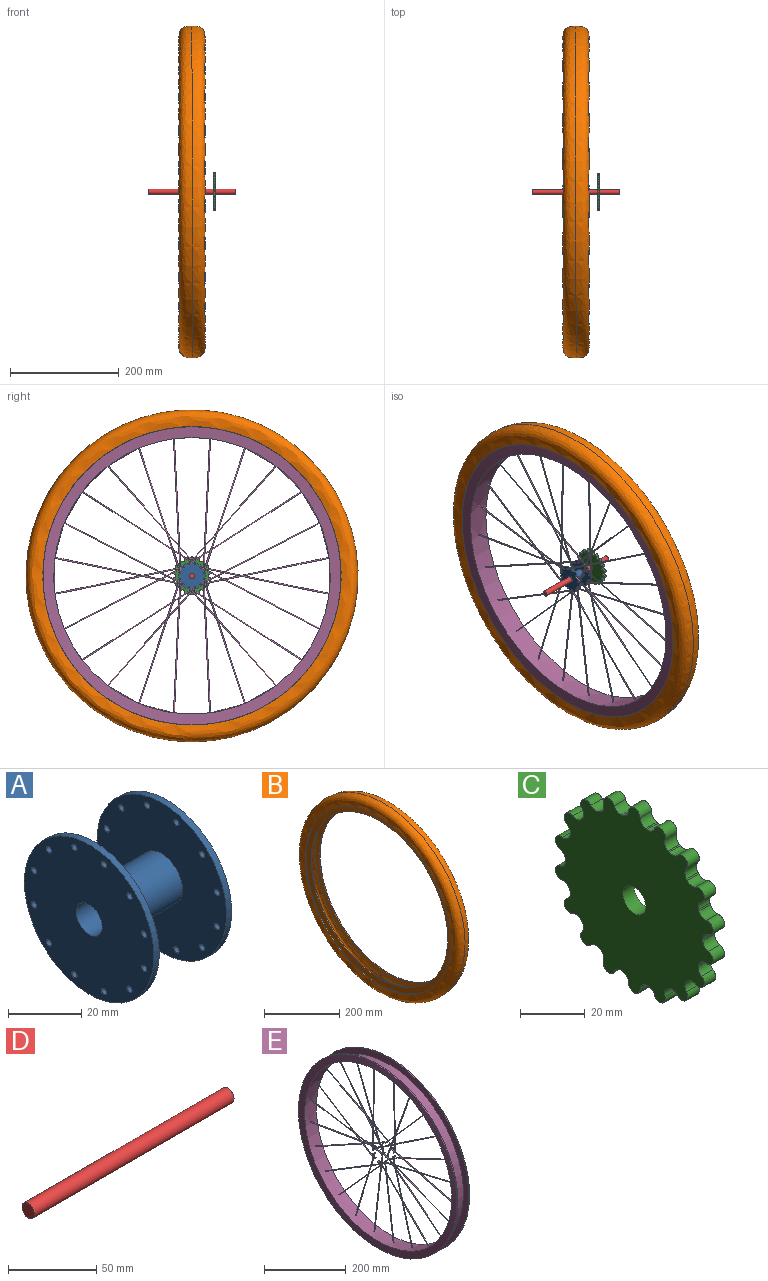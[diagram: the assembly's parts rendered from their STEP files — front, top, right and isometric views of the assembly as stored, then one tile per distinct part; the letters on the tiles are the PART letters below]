
ASSEMBLY  parts=5 mates=4
PART A: 32 faces, bbox 30x50x50 mm
  f0: cylinder r=8mm len=26mm, axis (-1,0,0), area 1306.9mm2, adj f4,f19
  f1: cylinder r=5mm len=30mm, axis (-1,0,0), area 942.5mm2, adj f2,f17
  f2: plane 50x50mm, normal (1,0,0), area 1847.3mm2, adj f1,f3,f5,f6,f7,f8,f9,f10
  f3: cylinder r=25mm len=50mm, axis (1,0,0), area 314.2mm2, adj f2,f4
  f4: plane 50x50mm, normal (-1,0,0), area 1724.7mm2, adj f0,f3,f5,f6,f7,f8,f9,f10
  f5: cylinder r=1mm len=2mm, axis (1,0,0), area 12.6mm2, adj f2,f4
  f6: cylinder r=1mm len=2mm, axis (1,0,0), area 12.6mm2, adj f2,f4
  f7: cylinder r=1mm len=2mm, axis (1,0,0), area 12.6mm2, adj f2,f4
  f8: cylinder r=1mm len=2mm, axis (1,0,0), area 12.6mm2, adj f2,f4
  f9: cylinder r=1mm len=2mm, axis (1,0,0), area 12.6mm2, adj f2,f4
  f10: cylinder r=1mm len=2mm, axis (1,0,0), area 12.6mm2, adj f2,f4
  f11: cylinder r=1mm len=2mm, axis (1,0,0), area 12.6mm2, adj f2,f4
  f12: cylinder r=1mm len=2mm, axis (1,0,0), area 12.6mm2, adj f2,f4
  f13: cylinder r=1mm len=2mm, axis (1,0,0), area 12.6mm2, adj f2,f4
  f14: cylinder r=1mm len=2mm, axis (1,0,0), area 12.6mm2, adj f2,f4
  f15: cylinder r=1mm len=2mm, axis (1,0,0), area 12.6mm2, adj f2,f4
  f16: cylinder r=1mm len=2mm, axis (1,0,0), area 12.6mm2, adj f2,f4
  f17: plane 50x50mm, normal (-1,0,0), area 1847.3mm2, adj f1,f18,f20,f21,f22,f23,f24,f25
  f18: cylinder r=25mm len=50mm, axis (-1,0,0), area 314.2mm2, adj f17,f19
  f19: plane 50x50mm, normal (1,0,0), area 1724.7mm2, adj f0,f18,f20,f21,f22,f23,f24,f25
  f20: cylinder r=1mm len=2mm, axis (-1,0,0), area 12.6mm2, adj f17,f19
  f21: cylinder r=1mm len=2mm, axis (-1,0,0), area 12.6mm2, adj f17,f19
  f22: cylinder r=1mm len=2mm, axis (-1,0,0), area 12.6mm2, adj f17,f19
  f23: cylinder r=1mm len=2mm, axis (-1,0,0), area 12.6mm2, adj f17,f19
  f24: cylinder r=1mm len=2mm, axis (-1,0,0), area 12.6mm2, adj f17,f19
  f25: cylinder r=1mm len=2mm, axis (-1,0,0), area 12.6mm2, adj f17,f19
  f26: cylinder r=1mm len=2mm, axis (-1,0,0), area 12.6mm2, adj f17,f19
  f27: cylinder r=1mm len=2mm, axis (-1,0,0), area 12.6mm2, adj f17,f19
  f28: cylinder r=1mm len=2mm, axis (-1,0,0), area 12.6mm2, adj f17,f19
  f29: cylinder r=1mm len=2mm, axis (-1,0,0), area 12.6mm2, adj f17,f19
  f30: cylinder r=1mm len=2mm, axis (-1,0,0), area 12.6mm2, adj f17,f19
  f31: cylinder r=1mm len=2mm, axis (-1,0,0), area 12.6mm2, adj f17,f19
PART B: 12 faces, bbox 48.1x610x610 mm
  f0: cone r=274.19mm half-angle=85deg, axis (-1,0,0), area 28787.9mm2, adj f1,f9
  f1: cylinder r=257mm len=514mm, axis (1,0,0), area 4862.8mm2, adj f0,f2
  f2: cone r=274.45mm half-angle=85deg, axis (-1,0,0), area 29240.3mm2, adj f1,f3
  f3: revolved ~598x598mm, area 68230.7mm2, adj f2,f4
  f4: revolved ~598x598mm, area 68230.7mm2, adj f3,f5
  f5: cone r=274.45mm half-angle=85deg, axis (1,0,0), area 29240.3mm2, adj f4,f6
  f6: cylinder r=257mm len=514mm, axis (1,0,0), area 4862.8mm2, adj f5,f7
  f7: cone r=274.19mm half-angle=85deg, axis (1,0,0), area 28787.9mm2, adj f6,f10
  f8: revolved ~610x610mm, area 87460.3mm2, adj f9,f11
  f9: cone r=273.92mm half-angle=5deg, axis (1,0,0), area 5165.8mm2, adj f0,f8
  f10: cone r=274.19mm half-angle=5deg, axis (-1,0,0), area 5165.8mm2, adj f7,f11
  f11: revolved ~610x610mm, area 87460.3mm2, adj f8,f10
PART C: 75 faces, bbox 5x69x70 mm
  f0: cylinder r=2.5mm len=5mm, axis (-1,0,0), area 39.3mm2, adj f1,f71,f73,f74
  f1: cylinder r=2.95mm len=5mm, axis (-1,0,0), area 20.7mm2, adj f0,f2,f73,f74
  f2: cylinder r=30mm len=5mm, axis (-1,0,0), area 2.5mm2, adj f1,f3,f73,f74
  f3: cylinder r=2.95mm len=5mm, axis (-1,0,0), area 20.7mm2, adj f2,f4,f73,f74
  f4: cylinder r=2.5mm len=5mm, axis (-1,0,0), area 39.3mm2, adj f3,f5,f73,f74
  f5: cylinder r=2.95mm len=5mm, axis (-1,0,0), area 20.7mm2, adj f4,f6,f73,f74
  f6: cylinder r=30mm len=5mm, axis (-1,0,0), area 2.5mm2, adj f5,f7,f73,f74
  f7: cylinder r=2.95mm len=5mm, axis (-1,0,0), area 20.7mm2, adj f6,f8,f73,f74
  f8: cylinder r=2.5mm len=5mm, axis (-1,0,0), area 39.3mm2, adj f7,f9,f73,f74
  f9: cylinder r=2.95mm len=5mm, axis (-1,0,0), area 20.7mm2, adj f8,f10,f73,f74
  f10: cylinder r=30mm len=5mm, axis (-1,0,0), area 2.5mm2, adj f9,f11,f73,f74
  f11: cylinder r=2.95mm len=5mm, axis (-1,0,0), area 20.7mm2, adj f10,f12,f73,f74
  f12: cylinder r=2.5mm len=5mm, axis (-1,0,0), area 39.3mm2, adj f11,f13,f73,f74
  f13: cylinder r=2.95mm len=5mm, axis (-1,0,0), area 20.7mm2, adj f12,f14,f73,f74
  f14: cylinder r=30mm len=5mm, axis (-1,0,0), area 2.5mm2, adj f13,f15,f73,f74
  f15: cylinder r=2.95mm len=5mm, axis (-1,0,0), area 20.7mm2, adj f14,f16,f73,f74
  f16: cylinder r=2.5mm len=5mm, axis (-1,0,0), area 39.3mm2, adj f15,f17,f73,f74
  f17: cylinder r=2.95mm len=5mm, axis (-1,0,0), area 20.7mm2, adj f16,f18,f73,f74
  f18: cylinder r=30mm len=5mm, axis (-1,0,0), area 2.5mm2, adj f17,f19,f73,f74
  f19: cylinder r=2.95mm len=5mm, axis (-1,0,0), area 20.7mm2, adj f18,f20,f73,f74
  f20: cylinder r=2.5mm len=5mm, axis (-1,0,0), area 39.3mm2, adj f19,f21,f73,f74
  f21: cylinder r=2.95mm len=5mm, axis (-1,0,0), area 20.7mm2, adj f20,f22,f73,f74
  f22: cylinder r=30mm len=5mm, axis (-1,0,0), area 2.5mm2, adj f21,f23,f73,f74
  f23: cylinder r=2.95mm len=5mm, axis (-1,0,0), area 20.7mm2, adj f22,f24,f73,f74
  f24: cylinder r=2.5mm len=5mm, axis (-1,0,0), area 39.3mm2, adj f23,f25,f73,f74
  f25: cylinder r=2.95mm len=5mm, axis (-1,0,0), area 20.7mm2, adj f24,f26,f73,f74
  f26: cylinder r=30mm len=5mm, axis (-1,0,0), area 2.5mm2, adj f25,f27,f73,f74
  f27: cylinder r=2.95mm len=5mm, axis (-1,0,0), area 20.7mm2, adj f26,f28,f73,f74
  f28: cylinder r=2.5mm len=5mm, axis (-1,0,0), area 39.3mm2, adj f27,f29,f73,f74
  f29: cylinder r=2.95mm len=5mm, axis (-1,0,0), area 20.7mm2, adj f28,f30,f73,f74
  f30: cylinder r=30mm len=5mm, axis (-1,0,0), area 2.5mm2, adj f29,f31,f73,f74
  f31: cylinder r=2.95mm len=5mm, axis (-1,0,0), area 20.7mm2, adj f30,f32,f73,f74
  f32: cylinder r=2.5mm len=5mm, axis (-1,0,0), area 39.3mm2, adj f31,f33,f73,f74
  f33: cylinder r=2.95mm len=5mm, axis (-1,0,0), area 20.7mm2, adj f32,f34,f73,f74
  f34: cylinder r=30mm len=5mm, axis (-1,0,0), area 2.5mm2, adj f33,f35,f73,f74
  f35: cylinder r=2.95mm len=5mm, axis (-1,0,0), area 20.7mm2, adj f34,f36,f73,f74
  f36: cylinder r=2.5mm len=5mm, axis (-1,0,0), area 39.3mm2, adj f35,f37,f73,f74
  f37: cylinder r=2.95mm len=5mm, axis (-1,0,0), area 20.7mm2, adj f36,f38,f73,f74
  f38: cylinder r=30mm len=5mm, axis (-1,0,0), area 2.5mm2, adj f37,f39,f73,f74
  f39: cylinder r=2.95mm len=5mm, axis (-1,0,0), area 20.7mm2, adj f38,f40,f73,f74
  f40: cylinder r=2.5mm len=5mm, axis (-1,0,0), area 39.3mm2, adj f39,f41,f73,f74
  f41: cylinder r=2.95mm len=5mm, axis (-1,0,0), area 20.7mm2, adj f40,f42,f73,f74
  f42: cylinder r=30mm len=5mm, axis (-1,0,0), area 2.5mm2, adj f41,f43,f73,f74
  f43: cylinder r=2.95mm len=5mm, axis (-1,0,0), area 20.7mm2, adj f42,f44,f73,f74
  f44: cylinder r=2.5mm len=5mm, axis (-1,0,0), area 39.3mm2, adj f43,f45,f73,f74
  f45: cylinder r=2.95mm len=5mm, axis (-1,0,0), area 20.7mm2, adj f44,f46,f73,f74
  f46: cylinder r=30mm len=5mm, axis (-1,0,0), area 2.5mm2, adj f45,f47,f73,f74
  f47: cylinder r=2.95mm len=5mm, axis (-1,0,0), area 20.7mm2, adj f46,f48,f73,f74
  f48: cylinder r=2.5mm len=5mm, axis (-1,0,0), area 39.3mm2, adj f47,f49,f73,f74
  f49: cylinder r=2.95mm len=5mm, axis (-1,0,0), area 20.7mm2, adj f48,f50,f73,f74
  f50: cylinder r=30mm len=5mm, axis (-1,0,0), area 2.5mm2, adj f49,f51,f73,f74
  f51: cylinder r=2.95mm len=5mm, axis (-1,0,0), area 20.7mm2, adj f50,f52,f73,f74
  f52: cylinder r=2.5mm len=5mm, axis (-1,0,0), area 39.3mm2, adj f51,f53,f73,f74
  f53: cylinder r=2.95mm len=5mm, axis (-1,0,0), area 20.7mm2, adj f52,f54,f73,f74
  f54: cylinder r=30mm len=5mm, axis (-1,0,0), area 2.5mm2, adj f53,f55,f73,f74
  f55: cylinder r=2.95mm len=5mm, axis (-1,0,0), area 20.7mm2, adj f54,f56,f73,f74
  f56: cylinder r=2.5mm len=5mm, axis (-1,0,0), area 39.3mm2, adj f55,f57,f73,f74
  f57: cylinder r=2.95mm len=5mm, axis (-1,0,0), area 20.7mm2, adj f56,f58,f73,f74
  f58: cylinder r=30mm len=5mm, axis (-1,0,0), area 2.5mm2, adj f57,f59,f73,f74
  f59: cylinder r=2.95mm len=5mm, axis (-1,0,0), area 20.7mm2, adj f58,f60,f73,f74
  f60: cylinder r=2.5mm len=5mm, axis (-1,0,0), area 39.3mm2, adj f59,f61,f73,f74
  f61: cylinder r=2.95mm len=5mm, axis (-1,0,0), area 20.7mm2, adj f60,f62,f73,f74
  f62: cylinder r=30mm len=5mm, axis (-1,0,0), area 2.5mm2, adj f61,f63,f73,f74
  f63: cylinder r=2.95mm len=5mm, axis (-1,0,0), area 20.7mm2, adj f62,f64,f73,f74
  f64: cylinder r=2.5mm len=5mm, axis (-1,0,0), area 39.3mm2, adj f63,f65,f73,f74
  f65: cylinder r=2.95mm len=5mm, axis (-1,0,0), area 20.7mm2, adj f64,f66,f73,f74
  f66: cylinder r=30mm len=5mm, axis (-1,0,0), area 2.5mm2, adj f65,f67,f73,f74
  f67: cylinder r=2.95mm len=5mm, axis (-1,0,0), area 20.7mm2, adj f66,f68,f73,f74
  f68: cylinder r=2.5mm len=5mm, axis (-1,0,0), area 39.3mm2, adj f67,f69,f73,f74
  f69: cylinder r=2.95mm len=5mm, axis (-1,0,0), area 20.7mm2, adj f68,f70,f73,f74
  f70: cylinder r=30mm len=5mm, axis (-1,0,0), area 2.5mm2, adj f69,f71,f73,f74
  f71: cylinder r=2.95mm len=5mm, axis (-1,0,0), area 20.7mm2, adj f0,f70,f73,f74
  f72: cylinder r=5mm len=10mm, axis (-1,0,0), area 157.1mm2, adj f73,f74
  f73: plane 70x69.01mm, normal (1,0,0), area 3202.1mm2, adj f0,f1,f2,f3,f4,f5,f6,f7
  f74: plane 70x69.01mm, normal (-1,0,0), area 3202.1mm2, adj f0,f1,f2,f3,f4,f5,f6,f7
PART D: 3 faces, bbox 160x10x10 mm
  f0: cylinder r=5mm len=160mm, axis (-1,0,0), area 5026.5mm2, adj f1,f2
  f1: plane 10x10mm, normal (1,0,0), area 78.5mm2, adj f0
  f2: plane 10x10mm, normal (-1,0,0), area 78.5mm2, adj f0
PART E: 104 faces, bbox 43.5x548.4x548.4 mm
  f0: plane 2x2mm, normal (-1,0,0), area 3.1mm2, adj f1
  f1: cylinder r=1mm len=4mm, axis (1,0,0), area 25.1mm2, adj f0,f2
  f2: torus R=1.5mm, axis (0,-1,-0.05), area 15.5mm2, adj f1,f3
  f3: cylinder r=1mm len=244.8mm, axis (-0.07,-0.05,1), area 1542.1mm2, adj f2,f96
  f4: plane 2x2mm, normal (1,0,0), area 3.1mm2, adj f5
  f5: cylinder r=1mm len=4.5mm, axis (-1,0,0), area 28.3mm2, adj f4,f6
  f6: torus R=1.5mm, axis (0,-0.2,0.98), area 14.4mm2, adj f5,f7
  f7: cylinder r=1mm len=235.36mm, axis (-0.04,-0.98,-0.2), area 1508mm2, adj f6,f96
  f8: plane 2x2mm, normal (-1,0,0), area 3.1mm2, adj f9
  f9: cylinder r=1mm len=4mm, axis (1,0,0), area 25.1mm2, adj f8,f10
  f10: torus R=1.5mm, axis (0,-0.46,-0.89), area 15.5mm2, adj f9,f11
  f11: cylinder r=1mm len=218.73mm, axis (-0.07,-0.89,0.46), area 1542.1mm2, adj f10,f96
  f12: plane 2x2mm, normal (1,0,0), area 3.1mm2, adj f13
  f13: cylinder r=1mm len=4.5mm, axis (-1,0,0), area 28.3mm2, adj f12,f14
  f14: torus R=1.5mm, axis (0,-0.95,0.32), area 14.4mm2, adj f13,f15
  f15: cylinder r=1mm len=228.29mm, axis (-0.04,-0.31,-0.95), area 1508mm2, adj f14,f96
  f16: plane 2x2mm, normal (-1,0,0), area 3.1mm2, adj f17
  f17: cylinder r=1mm len=4mm, axis (1,0,0), area 25.1mm2, adj f16,f18
  f18: torus R=1.5mm, axis (0,0.54,-0.84), area 15.5mm2, adj f17,f19
  f19: cylinder r=1mm len=206.99mm, axis (-0.07,-0.84,-0.54), area 1542.1mm2, adj f18,f96
  f20: plane 2x2mm, normal (1,0,0), area 3.1mm2, adj f21
  f21: cylinder r=1mm len=4.5mm, axis (-1,0,0), area 28.3mm2, adj f20,f22
  f22: torus R=1.5mm, axis (0,-0.75,-0.66), area 14.4mm2, adj f21,f23
  f23: cylinder r=1mm len=180.62mm, axis (-0.04,0.66,-0.75), area 1508mm2, adj f22,f96
  f24: plane 2x2mm, normal (-1,0,0), area 3.1mm2, adj f25
  f25: cylinder r=1mm len=4mm, axis (1,0,0), area 25.1mm2, adj f24,f26
  f26: torus R=1.5mm, axis (0,1,0.05), area 15.5mm2, adj f25,f27
  f27: cylinder r=1mm len=244.8mm, axis (-0.07,0.05,-1), area 1542.1mm2, adj f26,f96
  f28: plane 2x2mm, normal (1,0,0), area 3.1mm2, adj f29
  f29: cylinder r=1mm len=4.5mm, axis (-1,0,0), area 28.3mm2, adj f28,f30
  f30: torus R=1.5mm, axis (0,0.2,-0.98), area 14.4mm2, adj f29,f31
  f31: cylinder r=1mm len=235.36mm, axis (-0.04,0.98,0.2), area 1508mm2, adj f30,f96
  f32: plane 2x2mm, normal (-1,0,0), area 3.1mm2, adj f33
  f33: cylinder r=1mm len=4mm, axis (1,0,0), area 25.1mm2, adj f32,f34
  f34: torus R=1.5mm, axis (0,0.46,0.89), area 15.5mm2, adj f33,f35
  f35: cylinder r=1mm len=218.73mm, axis (-0.07,0.89,-0.46), area 1542.1mm2, adj f34,f96
  f36: plane 2x2mm, normal (1,0,0), area 3.1mm2, adj f37
  f37: cylinder r=1mm len=4.5mm, axis (-1,0,0), area 28.3mm2, adj f36,f38
  f38: torus R=1.5mm, axis (0,0.95,-0.32), area 14.4mm2, adj f37,f39
  f39: cylinder r=1mm len=228.29mm, axis (-0.04,0.31,0.95), area 1508mm2, adj f38,f96
  f40: plane 2x2mm, normal (-1,0,0), area 3.1mm2, adj f41
  f41: cylinder r=1mm len=4mm, axis (1,0,0), area 25.1mm2, adj f40,f42
  f42: torus R=1.5mm, axis (0,-0.54,0.84), area 15.5mm2, adj f41,f43
  f43: cylinder r=1mm len=206.99mm, axis (-0.07,0.84,0.54), area 1542.1mm2, adj f42,f96
  f44: plane 2x2mm, normal (1,0,0), area 3.1mm2, adj f45
  f45: cylinder r=1mm len=4.5mm, axis (-1,0,0), area 28.3mm2, adj f44,f46
  f46: torus R=1.5mm, axis (0,0.75,0.66), area 14.4mm2, adj f45,f47
  f47: cylinder r=1mm len=180.62mm, axis (-0.04,-0.66,0.75), area 1508mm2, adj f46,f96
  f48: plane 2x2mm, normal (1,0,0), area 3.1mm2, adj f49
  f49: cylinder r=1mm len=4mm, axis (-1,0,0), area 25.1mm2, adj f48,f50
  f50: torus R=1.5mm, axis (0,1,-0.05), area 15.5mm2, adj f49,f51
  f51: cylinder r=1mm len=244.8mm, axis (0.07,0.05,1), area 1542.1mm2, adj f50,f96
  f52: plane 2x2mm, normal (-1,0,0), area 3.1mm2, adj f53
  f53: cylinder r=1mm len=4.5mm, axis (1,0,0), area 28.3mm2, adj f52,f54
  f54: torus R=1.5mm, axis (0,0.2,0.98), area 14.4mm2, adj f53,f55
  f55: cylinder r=1mm len=235.36mm, axis (0.04,0.98,-0.2), area 1508mm2, adj f54,f96
  f56: plane 2x2mm, normal (1,0,0), area 3.1mm2, adj f57
  f57: cylinder r=1mm len=4mm, axis (-1,0,0), area 25.1mm2, adj f56,f58
  f58: torus R=1.5mm, axis (0,0.46,-0.89), area 15.5mm2, adj f57,f59
  f59: cylinder r=1mm len=218.73mm, axis (0.07,0.89,0.46), area 1542.1mm2, adj f58,f96
  f60: plane 2x2mm, normal (-1,0,0), area 3.1mm2, adj f61
  f61: cylinder r=1mm len=4.5mm, axis (1,0,0), area 28.3mm2, adj f60,f62
  f62: torus R=1.5mm, axis (0,0.95,0.32), area 14.4mm2, adj f61,f63
  f63: cylinder r=1mm len=228.29mm, axis (0.04,0.31,-0.95), area 1508mm2, adj f62,f96
  f64: plane 2x2mm, normal (1,0,0), area 3.1mm2, adj f65
  f65: cylinder r=1mm len=4mm, axis (-1,0,0), area 25.1mm2, adj f64,f66
  f66: torus R=1.5mm, axis (0,-0.54,-0.84), area 15.5mm2, adj f65,f67
  f67: cylinder r=1mm len=206.99mm, axis (0.07,0.84,-0.54), area 1542.1mm2, adj f66,f96
  f68: plane 2x2mm, normal (-1,0,0), area 3.1mm2, adj f69
  f69: cylinder r=1mm len=4.5mm, axis (1,0,0), area 28.3mm2, adj f68,f70
  f70: torus R=1.5mm, axis (0,0.75,-0.66), area 14.4mm2, adj f69,f71
  f71: cylinder r=1mm len=180.62mm, axis (0.04,-0.66,-0.75), area 1508mm2, adj f70,f96
  f72: plane 2x2mm, normal (1,0,0), area 3.1mm2, adj f73
  f73: cylinder r=1mm len=4mm, axis (-1,0,0), area 25.1mm2, adj f72,f74
  f74: torus R=1.5mm, axis (0,-1,0.05), area 15.5mm2, adj f73,f75
  f75: cylinder r=1mm len=244.8mm, axis (0.07,-0.05,-1), area 1542.1mm2, adj f74,f96
  f76: plane 2x2mm, normal (-1,0,0), area 3.1mm2, adj f77
  f77: cylinder r=1mm len=4.5mm, axis (1,0,0), area 28.3mm2, adj f76,f78
  f78: torus R=1.5mm, axis (0,-0.2,-0.98), area 14.4mm2, adj f77,f79
  f79: cylinder r=1mm len=235.36mm, axis (0.04,-0.98,0.2), area 1508mm2, adj f78,f96
  f80: plane 2x2mm, normal (1,0,0), area 3.1mm2, adj f81
  f81: cylinder r=1mm len=4mm, axis (-1,0,0), area 25.1mm2, adj f80,f82
  f82: torus R=1.5mm, axis (0,-0.46,0.89), area 15.5mm2, adj f81,f83
  f83: cylinder r=1mm len=218.73mm, axis (0.07,-0.89,-0.46), area 1542.1mm2, adj f82,f96
  f84: plane 2x2mm, normal (-1,0,0), area 3.1mm2, adj f85
  f85: cylinder r=1mm len=4.5mm, axis (1,0,0), area 28.3mm2, adj f84,f86
  f86: torus R=1.5mm, axis (0,-0.95,-0.32), area 14.4mm2, adj f85,f87
  f87: cylinder r=1mm len=228.29mm, axis (0.04,-0.31,0.95), area 1508mm2, adj f86,f96
  f88: plane 2x2mm, normal (1,0,0), area 3.1mm2, adj f89
  f89: cylinder r=1mm len=4mm, axis (-1,0,0), area 25.1mm2, adj f88,f90
  f90: torus R=1.5mm, axis (0,0.54,0.84), area 15.5mm2, adj f89,f91
  f91: cylinder r=1mm len=206.99mm, axis (0.07,-0.84,0.54), area 1542.1mm2, adj f90,f96
  f92: plane 2x2mm, normal (-1,0,0), area 3.1mm2, adj f93
  f93: cylinder r=1mm len=4.5mm, axis (1,0,0), area 28.3mm2, adj f92,f94
  f94: torus R=1.5mm, axis (0,-0.75,0.66), area 14.4mm2, adj f93,f95
  f95: cylinder r=1mm len=180.62mm, axis (0.04,0.66,0.75), area 1508mm2, adj f94,f96
  f96: cylinder r=254mm len=508mm, axis (-1,0,0), area 63761.5mm2, adj f3,f7,f11,f15,f19,f23,f27,f31
  f97: cone r=254mm half-angle=85deg, axis (1,0,0), area 33170.4mm2, adj f96,f98
  f98: cone r=273.92mm half-angle=5deg, axis (-1,0,0), area 5165.8mm2, adj f97,f99
  f99: cone r=274.19mm half-angle=85deg, axis (1,0,0), area 28787.9mm2, adj f98,f100
  f100: cylinder r=257mm len=514mm, axis (-1,0,0), area 55713.1mm2, adj f99,f101
  f101: cone r=274.19mm half-angle=85deg, axis (-1,0,0), area 28787.9mm2, adj f100,f102
  f102: cone r=273.92mm half-angle=5deg, axis (1,0,0), area 5165.8mm2, adj f101,f103
  f103: cone r=254mm half-angle=85deg, axis (-1,0,0), area 33170.4mm2, adj f96,f102
PLACE A t=(-14.48,-2.32,0.4)mm
PLACE B t=(-14.48,-2.32,0.4)mm
PLACE C t=(-35.48,-802.32,0.4)mm
PLACE D t=(-30.48,-802.32,0.4)mm
PLACE E t=(-14.48,-2.32,0.4)mm
MATE fastened D.f0 <-> C.f72  axis (1,0,0) through (65.52,-2.32,0.4)mm
MATE fastened A.f0 <-> D.f0  axis (-1,0,0) through (-14.48,-2.32,0.4)mm
MATE fastened B.f0 <-> E.f96  axis (1,0,0) through (3.53,-2.32,0.4)mm
MATE fastened E.f41 <-> A.f16  axis (-1,0,0) through (-2.48,-8.01,21.65)mm
